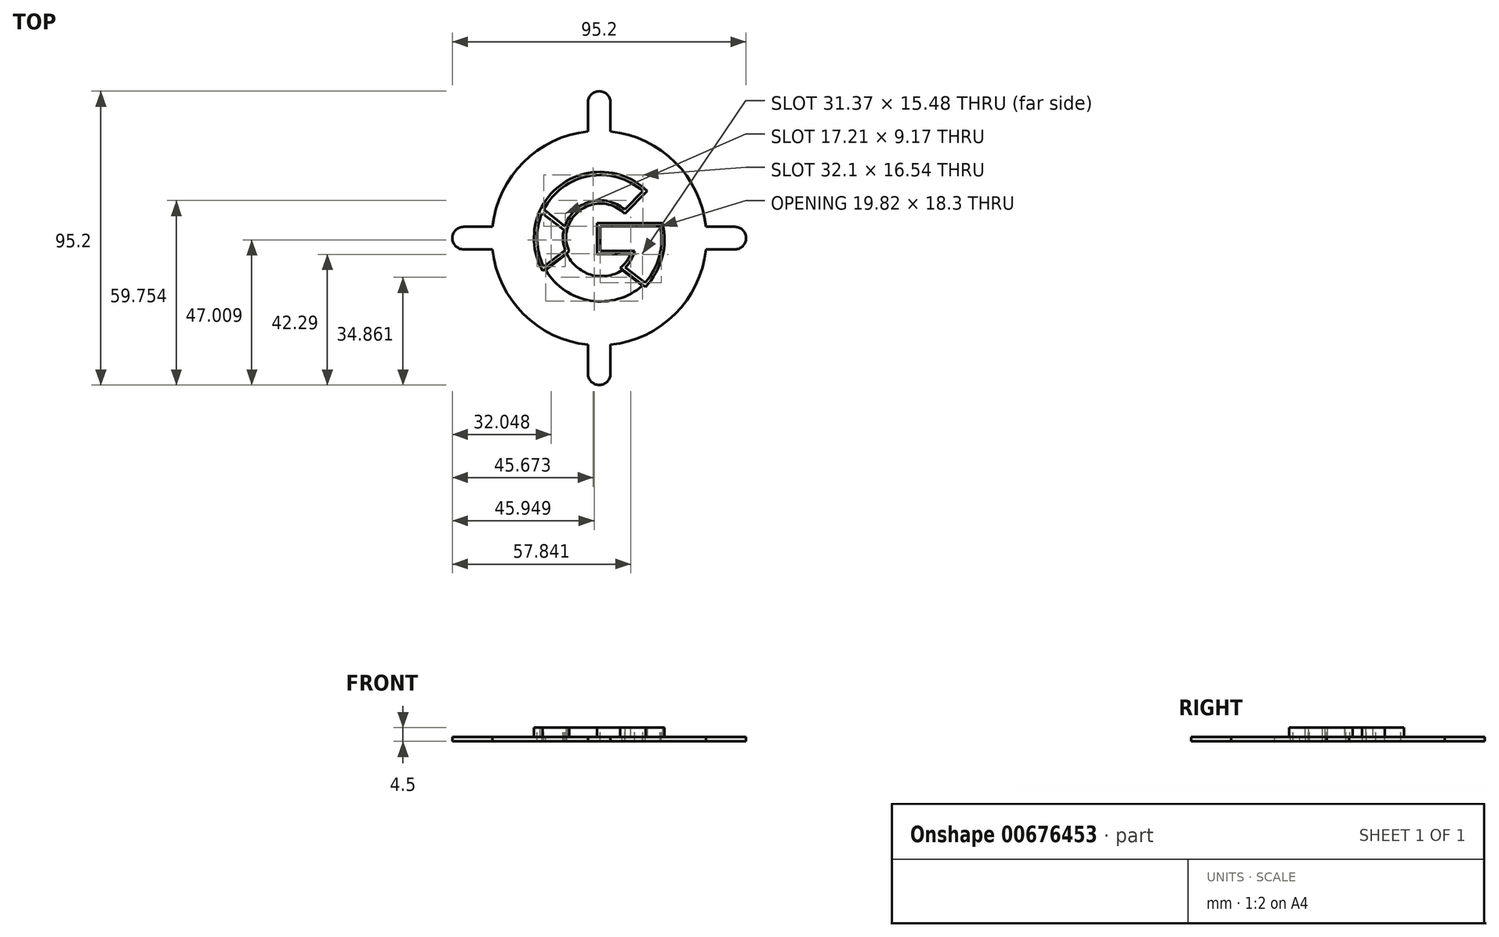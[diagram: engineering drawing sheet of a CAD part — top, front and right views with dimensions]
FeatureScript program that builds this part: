
annotation { "Feature Type Name" : "Feature", "Feature Type Description" : "" }
export const myFeature = defineFeature(function(context is Context, id is Id, definition is map)
    precondition{}
    {
        {
            var Q0;
            Q0=qCreatedBy(makeId("Top.planeOp"),FACE);
            var sketch = newSketch(context, id + "F0", { "sketchPlane" : qUnion([Q0])});
            skCircle(sketch, "E0", {"center": v(0, 0) * mm, "radius": 69.53 * mm});
            skLineSegment(sketch, "E1", {"start": v(-7.31, 69.15) * mm, "end": v(-7.31, 87.88) * mm});
            skPoint(sketch, "E2", {"position": v(0, 69.53) * mm});
            skArc(sketch, "E3", {"start": v(-7.31, 87.88) * mm, "mid": v(-5.17, 93.06) * mm, "end": v(0, 95.2) * mm});
            skLineSegment(sketch, "E4.MirrorCS", {"start": v(7.31, 69.15) * mm, "end": v(7.31, 87.88) * mm});
            skArc(sketch, "E5.MirrorCS", {"start": v(7.31, 87.88) * mm, "mid": v(5.17, 93.06) * mm, "end": v(0, 95.2) * mm});
            skLineSegment(sketch, "E6.1.0", {"start": v(-69.15, -7.31) * mm, "end": v(-87.88, -7.31) * mm});
            skArc(sketch, "E6.1.1", {"start": v(-87.88, -7.31) * mm, "mid": v(-93.06, -5.17) * mm, "end": v(-95.2, 0) * mm});
            skArc(sketch, "E6.1.2", {"start": v(-87.88, 7.31) * mm, "mid": v(-93.06, 5.17) * mm, "end": v(-95.2, 0) * mm});
            skLineSegment(sketch, "E6.1.3", {"start": v(-69.15, 7.31) * mm, "end": v(-87.88, 7.31) * mm});
            skLineSegment(sketch, "E6.2.0", {"start": v(7.31, -69.15) * mm, "end": v(7.31, -87.88) * mm});
            skArc(sketch, "E6.2.1", {"start": v(7.31, -87.88) * mm, "mid": v(5.17, -93.06) * mm, "end": v(0, -95.2) * mm});
            skArc(sketch, "E6.2.2", {"start": v(-7.31, -87.88) * mm, "mid": v(-5.17, -93.06) * mm, "end": v(0, -95.2) * mm});
            skLineSegment(sketch, "E6.2.3", {"start": v(-7.31, -69.15) * mm, "end": v(-7.31, -87.88) * mm});
            skLineSegment(sketch, "E6.3.0", {"start": v(69.15, 7.31) * mm, "end": v(87.88, 7.31) * mm});
            skArc(sketch, "E6.3.1", {"start": v(87.88, 7.31) * mm, "mid": v(93.06, 5.17) * mm, "end": v(95.2, 0) * mm});
            skArc(sketch, "E6.3.2", {"start": v(87.88, -7.31) * mm, "mid": v(93.06, -5.17) * mm, "end": v(95.2, 0) * mm});
            skLineSegment(sketch, "E6.3.3", {"start": v(69.15, -7.31) * mm, "end": v(87.88, -7.31) * mm});
            skSolve(sketch);
        }
        {
            var Q0;
            Q0=qSketchRegion(id+"F0",true);
            extrude(context, id + "F1", {"entities" : qUnion([Q0]), "depth" : 3 * mm, "offsetDistance" : 25 * mm});
        }
        {
            var Q0;
            Q0=makeQuery(id+"F1.opExtrude","CAP_FACE",FACE,{"disambiguationData":[OSD([sQuery(id+"F0.wireOp",EDGE,"E0"),sQuery(id+"F0.wireOp",EDGE,"E1"),sQuery(id+"F0.wireOp",EDGE,"E3"),sQuery(id+"F0.wireOp",EDGE,"E4.MirrorCS"),sQuery(id+"F0.wireOp",EDGE,"E5.MirrorCS"),sQuery(id+"F0.wireOp",EDGE,"E6.1.0"),sQuery(id+"F0.wireOp",EDGE,"E6.1.1"),sQuery(id+"F0.wireOp",EDGE,"E6.1.2"),sQuery(id+"F0.wireOp",EDGE,"E6.1.3"),sQuery(id+"F0.wireOp",EDGE,"E6.2.0"),sQuery(id+"F0.wireOp",EDGE,"E6.2.1"),sQuery(id+"F0.wireOp",EDGE,"E6.2.2"),sQuery(id+"F0.wireOp",EDGE,"E6.2.3"),sQuery(id+"F0.wireOp",EDGE,"E6.3.0"),sQuery(id+"F0.wireOp",EDGE,"E6.3.1"),sQuery(id+"F0.wireOp",EDGE,"E6.3.2"),sQuery(id+"F0.wireOp",EDGE,"E6.3.3")])],"isStart":false});
            var sketch = newSketch(context, id + "F2", { "sketchPlane" : qUnion([Q0])});
            skLineSegment(sketch, "E7", {"start": v(59, 59) * mm, "end": v(-59, -59) * mm, "construction": true});
            skPoint(sketch, "E8", {"position": v(0, 0) * mm});
            skPoint(sketch, "E9", {"position": v(28.24, 30.42) * mm});
            skPoint(sketch, "E10", {"position": v(16.52, 18.5) * mm});
            skPoint(sketch, "E11", {"position": v(-22.14, 7.77) * mm});
            skPoint(sketch, "E12", {"position": v(-35.95, 18.5) * mm});
            skLineSegment(sketch, "E13", {"start": v(28.24, 30.42) * mm, "end": v(16.52, 18.5) * mm});
            skLineSegment(sketch, "E14", {"start": v(-35.95, 18.5) * mm, "end": v(-22.14, 7.77) * mm});
            skArc(sketch, "E15", {"start": v(28.24, 30.42) * mm, "mid": v(-6.78, 40.2) * mm, "end": v(-35.95, 18.5) * mm});
            skArc(sketch, "E16", {"start": v(16.52, 18.5) * mm, "mid": v(-5.7, 23.57) * mm, "end": v(-22.14, 7.77) * mm});
            skPoint(sketch, "E17", {"position": v(-36, -18.4) * mm});
            skPoint(sketch, "E18", {"position": v(-21.94, -7.77) * mm});
            skPoint(sketch, "E19", {"position": v(14.72, -20.89) * mm});
            skPoint(sketch, "E20", {"position": v(28.07, -30.83) * mm});
            skPoint(sketch, "E21", {"position": v(22.87, -8.26) * mm});
            skPoint(sketch, "E22", {"position": v(0.66, -8.26) * mm});
            skPoint(sketch, "E23", {"position": v(0.66, 7.68) * mm});
            skPoint(sketch, "E24", {"position": v(39.44, 7.68) * mm});
            skLineSegment(sketch, "E25", {"start": v(22.87, -8.26) * mm, "end": v(0.66, -8.26) * mm});
            skLineSegment(sketch, "E26", {"start": v(0.66, 7.68) * mm, "end": v(39.44, 7.68) * mm});
            skLineSegment(sketch, "E27", {"start": v(0.66, 7.68) * mm, "end": v(0.66, -8.26) * mm});
            skArc(sketch, "E28", {"start": v(-22.93, 5.33) * mm, "mid": v(-23.5, -1.3) * mm, "end": v(-21.94, -7.77) * mm});
            skArc(sketch, "E29", {"start": v(-37.08, 16.03) * mm, "mid": v(-40.27, -1.3) * mm, "end": v(-36, -18.4) * mm});
            skArc(sketch, "E30", {"start": v(-34.67, -20.8) * mm, "mid": v(-5.65, -40.51) * mm, "end": v(28.07, -30.83) * mm});
            skArc(sketch, "E31", {"start": v(-21.08, -10) * mm, "mid": v(-5.67, -23.64) * mm, "end": v(14.72, -20.89) * mm});
            skArc(sketch, "E32", {"start": v(16.86, -19.1) * mm, "mid": v(20.68, -14.13) * mm, "end": v(22.87, -8.26) * mm});
            skArc(sketch, "E33", {"start": v(30.53, -28.1) * mm, "mid": v(39.05, -11.22) * mm, "end": v(39.44, 7.68) * mm});
            skLineSegment(sketch, "E34", {"start": v(-37.08, 16.03) * mm, "end": v(-22.93, 5.33) * mm});
            skLineSegment(sketch, "E35", {"start": v(-34.67, -20.8) * mm, "end": v(-21.08, -10) * mm});
            skLineSegment(sketch, "E36", {"start": v(-36, -18.4) * mm, "end": v(-21.94, -7.77) * mm});
            skLineSegment(sketch, "E37", {"start": v(14.72, -20.89) * mm, "end": v(28.07, -30.83) * mm});
            skArc(sketch, "E38", {"start": v(29.83, -28.92) * mm, "mid": v(30.18, -28.5) * mm, "end": v(30.53, -28.1) * mm});
            skLineSegment(sketch, "E39", {"start": v(16.86, -19.1) * mm, "end": v(29.83, -28.92) * mm});
            skSolve(sketch);
        }
        {
            var Q0;
            Q0 = qSketchRegion(id + "F2", true);
            extrude(context, id + "F3", {"entities" : qUnion([Q0]), "operationType" : NewBodyOperationType.REMOVE, "oppositeDirection" : true, "depth" : 25 * mm, "offsetDistance" : 25 * mm});
        }
        {
            var Q0;
            Q0=makeQuery(id+"F1.opExtrude","CAP_FACE",FACE,{"disambiguationData":[OSD([sQuery(id+"F0.wireOp",EDGE,"E0"),sQuery(id+"F0.wireOp",EDGE,"E1"),sQuery(id+"F0.wireOp",EDGE,"E3"),sQuery(id+"F0.wireOp",EDGE,"E4.MirrorCS"),sQuery(id+"F0.wireOp",EDGE,"E5.MirrorCS"),sQuery(id+"F0.wireOp",EDGE,"E6.1.0"),sQuery(id+"F0.wireOp",EDGE,"E6.1.1"),sQuery(id+"F0.wireOp",EDGE,"E6.1.2"),sQuery(id+"F0.wireOp",EDGE,"E6.1.3"),sQuery(id+"F0.wireOp",EDGE,"E6.2.0"),sQuery(id+"F0.wireOp",EDGE,"E6.2.1"),sQuery(id+"F0.wireOp",EDGE,"E6.2.2"),sQuery(id+"F0.wireOp",EDGE,"E6.2.3"),sQuery(id+"F0.wireOp",EDGE,"E6.3.0"),sQuery(id+"F0.wireOp",EDGE,"E6.3.1"),sQuery(id+"F0.wireOp",EDGE,"E6.3.2"),sQuery(id+"F0.wireOp",EDGE,"E6.3.3")])],"isStart":false});
            var sketch = newSketch(context, id + "F4", { "sketchPlane" : qUnion([Q0])});
            skArc(sketch, "E40.0", {"start": v(31.1, 30.48) * mm, "mid": v(-6.93, 42.2) * mm, "end": v(-38.46, 17.92) * mm});
            skLineSegment(sketch, "E40.1", {"start": v(31.1, 30.48) * mm, "end": v(16.56, 15.7) * mm});
            skArc(sketch, "E40.2", {"start": v(16.56, 15.7) * mm, "mid": v(-5.68, 21.5) * mm, "end": v(-20.94, 4.3) * mm});
            skLineSegment(sketch, "E40.3", {"start": v(-38.46, 17.92) * mm, "end": v(-20.94, 4.3) * mm});
            skArc(sketch, "E41.0", {"start": v(28.24, 30.42) * mm, "mid": v(-6.78, 40.2) * mm, "end": v(-35.95, 18.5) * mm});
            skLineSegment(sketch, "E42.0", {"start": v(-35.95, 18.5) * mm, "end": v(-22.14, 7.77) * mm});
            skArc(sketch, "E43.0", {"start": v(16.52, 18.5) * mm, "mid": v(-5.7, 23.57) * mm, "end": v(-22.14, 7.77) * mm});
            skPoint(sketch, "E44.0", {"position": v(22.38, 24.46) * mm});
            skLineSegment(sketch, "E45.0", {"start": v(28.24, 30.42) * mm, "end": v(16.52, 18.5) * mm});
            skLineSegment(sketch, "E46.0", {"start": v(-37.87, 19.13) * mm, "end": v(-20.62, 6.1) * mm});
            skArc(sketch, "E46.1", {"start": v(-37.87, 19.13) * mm, "mid": v(-42.27, -1.29) * mm, "end": v(-36.66, -21.4) * mm});
            skLineSegment(sketch, "E46.2", {"start": v(-36.66, -21.4) * mm, "end": v(-19.43, -8.39) * mm});
            skArc(sketch, "E46.3", {"start": v(-21.09, 4.42) * mm, "mid": v(-21.4, -2.13) * mm, "end": v(-19.43, -8.39) * mm});
            skLineSegment(sketch, "E47", {"start": v(-20.94, 4.3) * mm, "end": v(-20.94, 4.3) * mm});
            skLineSegment(sketch, "E48.0", {"start": v(-36, -18.4) * mm, "end": v(-21.94, -7.77) * mm});
            skArc(sketch, "E49.0", {"start": v(-22.93, 5.33) * mm, "mid": v(-23.5, -1.3) * mm, "end": v(-21.94, -7.77) * mm});
            skArc(sketch, "E50.0", {"start": v(-37.08, 16.03) * mm, "mid": v(-40.27, -1.3) * mm, "end": v(-36, -18.4) * mm});
            skLineSegment(sketch, "E51.0", {"start": v(-37.08, 16.03) * mm, "end": v(-22.93, 5.33) * mm});
            skArc(sketch, "E52.0", {"start": v(-37.25, -20.3) * mm, "mid": v(-5.62, -42.54) * mm, "end": v(31.2, -30.66) * mm});
            skLineSegment(sketch, "E52.1", {"start": v(-37.25, -20.3) * mm, "end": v(-20.17, -6.73) * mm});
            skArc(sketch, "E52.2", {"start": v(-20.17, -6.73) * mm, "mid": v(-5.7, -21.54) * mm, "end": v(14.78, -18.43) * mm});
            skLineSegment(sketch, "E52.3", {"start": v(14.78, -18.43) * mm, "end": v(31.2, -30.66) * mm});
            skArc(sketch, "E53.0", {"start": v(13.66, -19.18) * mm, "mid": v(17.61, -15.2) * mm, "end": v(20.24, -10.26) * mm});
            skArc(sketch, "E53.1", {"start": v(30.09, -31.61) * mm, "mid": v(40.82, -12.36) * mm, "end": v(41.04, 9.68) * mm});
            skLineSegment(sketch, "E53.2", {"start": v(-1.34, 9.68) * mm, "end": v(41.04, 9.68) * mm});
            skLineSegment(sketch, "E53.3", {"start": v(13.66, -19.18) * mm, "end": v(30.09, -31.61) * mm});
            skLineSegment(sketch, "E53.4", {"start": v(-1.34, 9.68) * mm, "end": v(-1.34, -10.26) * mm});
            skLineSegment(sketch, "E53.5", {"start": v(20.24, -10.26) * mm, "end": v(-1.34, -10.26) * mm});
            skSolve(sketch);
        }
        {
            var Q0;
            {var subQ1=sQuery(id+"F4.wireOp",EDGE,"E40.0");Q0=makeQuery(id+"F4.imprint","IMPRINT",FACE,{"disambiguationData":[TD([[makeQuery(id+"F4.imprint","IMPRINT",EDGE,{"derivedFrom":subQ1}),1.0]])]});}
            var Q1;
            Q1=makeQuery(id+"F4.imprint","IMPRINT",FACE,{"disambiguationData":[TD([[makeQuery(id+"F4.imprint","IMPRINT",EDGE,{"derivedFrom":makeQuery(id+"F3.boolean.opBoolean","COPY",EDGE,{"derivedFrom":makeQuery(id+"F3.opExtrude","CAP_EDGE",EDGE,{"disambiguationData":[OSD([sQuery(id+"F2.wireOp",EDGE,"E30")])],"isStart":true})})}),-1.0]])]});
            var Q2;
            Q2=makeQuery(id+"F4.imprint","IMPRINT",FACE,{"disambiguationData":[TD([[makeQuery(id+"F4.imprint","IMPRINT",EDGE,{"derivedFrom":sQuery(id+"F4.wireOp",EDGE,"E48.0")}),-1.0]])]});
            var Q3;
            {var subQ1=sQuery(id+"F4.wireOp",EDGE,"E52.0");var subQ5=sQuery(id+"F4.wireOp",EDGE,"E46.2");var subQ6=makeQuery(id+"F4.imprint","INTERSECT",VERTEX,{"derivedFrom":[subQ5,subQ1]});Q3=makeQuery(id+"F4.imprint","IMPRINT",FACE,{"disambiguationData":[TD([[makeQuery(id+"F4.imprint","IMPRINT",EDGE,{"disambiguationData":[TD([[subQ6,-1.0]])],"derivedFrom":subQ5}),1.0]])]});}
            var Q4;
            {var subQ0=sQuery(id+"F4.wireOp",EDGE,"E52.3");var subQ1=sQuery(id+"F4.wireOp",EDGE,"E52.2");var subQ2=makeQuery(id+"F4.imprint","INTERSECT",VERTEX,{"derivedFrom":[subQ1,subQ0]});Q4=makeQuery(id+"F4.imprint","IMPRINT",FACE,{"disambiguationData":[TD([[makeQuery(id+"F4.imprint","IMPRINT",EDGE,{"disambiguationData":[TD([[subQ2,1.0]])],"derivedFrom":subQ1}),-1.0]])]});}
            var Q5;
            {var subQ1=sQuery(id+"F4.wireOp",EDGE,"E53.0");Q5=makeQuery(id+"F4.imprint","IMPRINT",FACE,{"disambiguationData":[TD([[makeQuery(id+"F4.imprint","IMPRINT",EDGE,{"derivedFrom":subQ1}),-1.0]])]});}
            extrude(context, id + "F5", {"entities" : qUnion([Q0, Q1, Q2, Q3, Q4, Q5]), "operationType" : NewBodyOperationType.ADD, "depth" : 6 * mm, "offsetDistance" : 25 * mm});
        }
        {
            var Q0;
            Q0=makeQuery(id+"F1.opExtrude","SWEPT_BODY",BODY,{"disambiguationData":[OSD([sQuery(id+"F0.wireOp",EDGE,"E0"),sQuery(id+"F0.wireOp",EDGE,"E1"),sQuery(id+"F0.wireOp",EDGE,"E3"),sQuery(id+"F0.wireOp",EDGE,"E4.MirrorCS"),sQuery(id+"F0.wireOp",EDGE,"E5.MirrorCS"),sQuery(id+"F0.wireOp",EDGE,"E6.1.0"),sQuery(id+"F0.wireOp",EDGE,"E6.1.1"),sQuery(id+"F0.wireOp",EDGE,"E6.1.2"),sQuery(id+"F0.wireOp",EDGE,"E6.1.3"),sQuery(id+"F0.wireOp",EDGE,"E6.2.0"),sQuery(id+"F0.wireOp",EDGE,"E6.2.1"),sQuery(id+"F0.wireOp",EDGE,"E6.2.2"),sQuery(id+"F0.wireOp",EDGE,"E6.2.3"),sQuery(id+"F0.wireOp",EDGE,"E6.3.0"),sQuery(id+"F0.wireOp",EDGE,"E6.3.1"),sQuery(id+"F0.wireOp",EDGE,"E6.3.2"),sQuery(id+"F0.wireOp",EDGE,"E6.3.3")])]});
            var Q1;
            Q1=qCreatedBy(makeId("Origin.pointOp"),VERTEX);
            var Q2;
            Q2=qCreatedBy(makeId("Origin.pointOp"),VERTEX);
            transform(context, id + "F6", {"entities" : qUnion([Q0]), "transformType" : TransformType.SCALE_UNIFORMLY, "scale" : .5, "scalePoint" : qUnion([Q2]), "makeCopy" : false});
        }
    });
